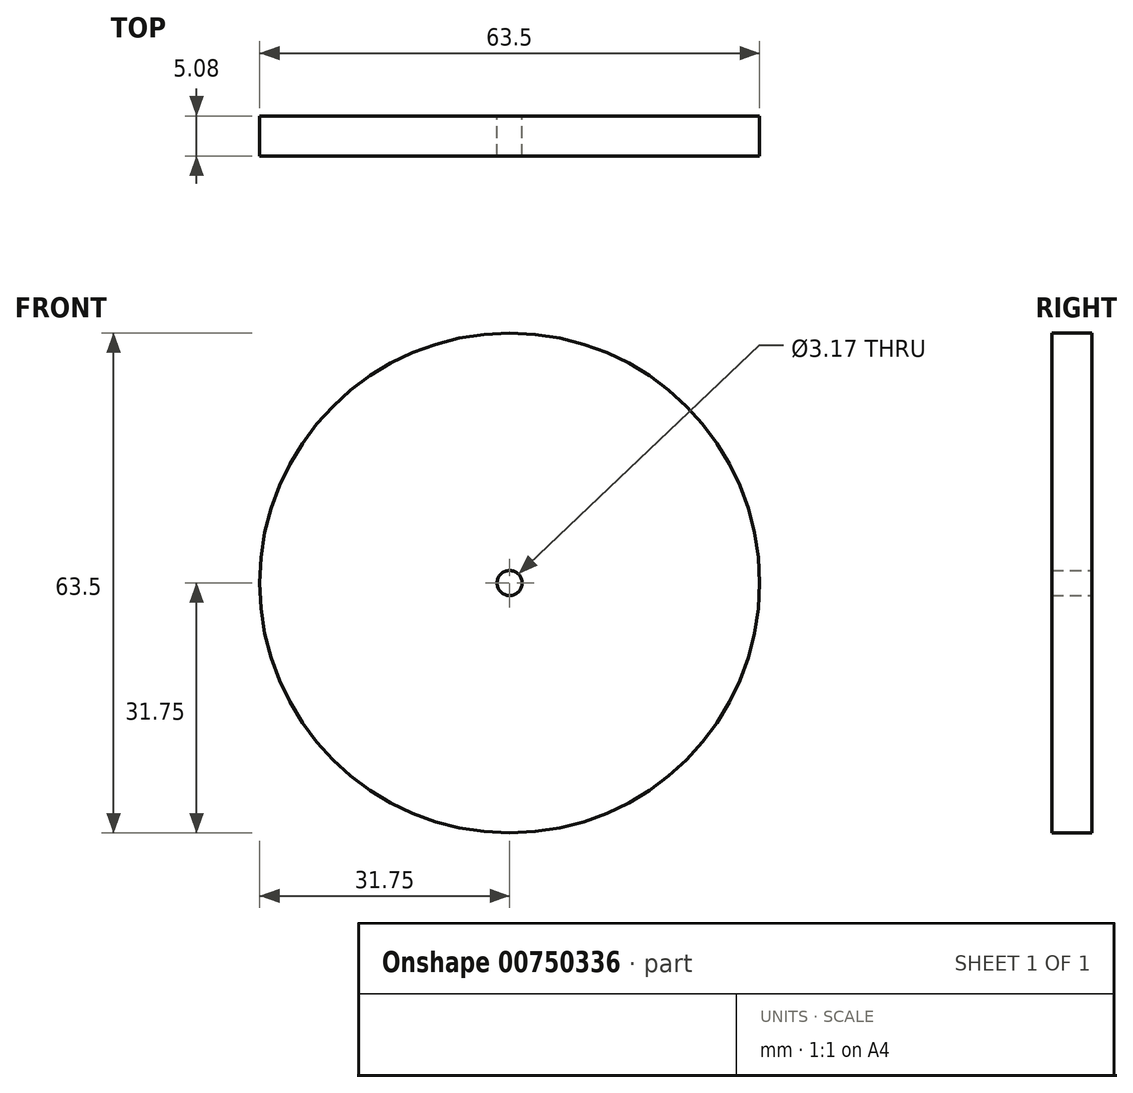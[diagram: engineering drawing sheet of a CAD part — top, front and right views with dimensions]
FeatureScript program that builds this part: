
annotation { "Feature Type Name" : "Feature", "Feature Type Description" : "" }
export const myFeature = defineFeature(function(context is Context, id is Id, definition is map)
    precondition{}
    {
        {
            var Q0;
            Q0=qCreatedBy(makeId("Front.planeOp"),FACE);
            var sketch = newSketch(context, id + "F0", { "sketchPlane" : qUnion([Q0])});
            skCircle(sketch, "E0", {"center": v(0, 0) * mm, "radius": 31.75 * mm});
            skCircle(sketch, "E1", {"center": v(0, 0) * mm, "radius": 1.59 * mm});
            skSolve(sketch);
        }
        {
            var Q0;
            Q0 = qSketchRegion(id + "F0", true);
            extrude(context, id + "F1", {"entities" : qUnion([Q0]), "depth" : 5.08 * mm, "offsetDistance" : 25.4 * mm});
        }
    });
